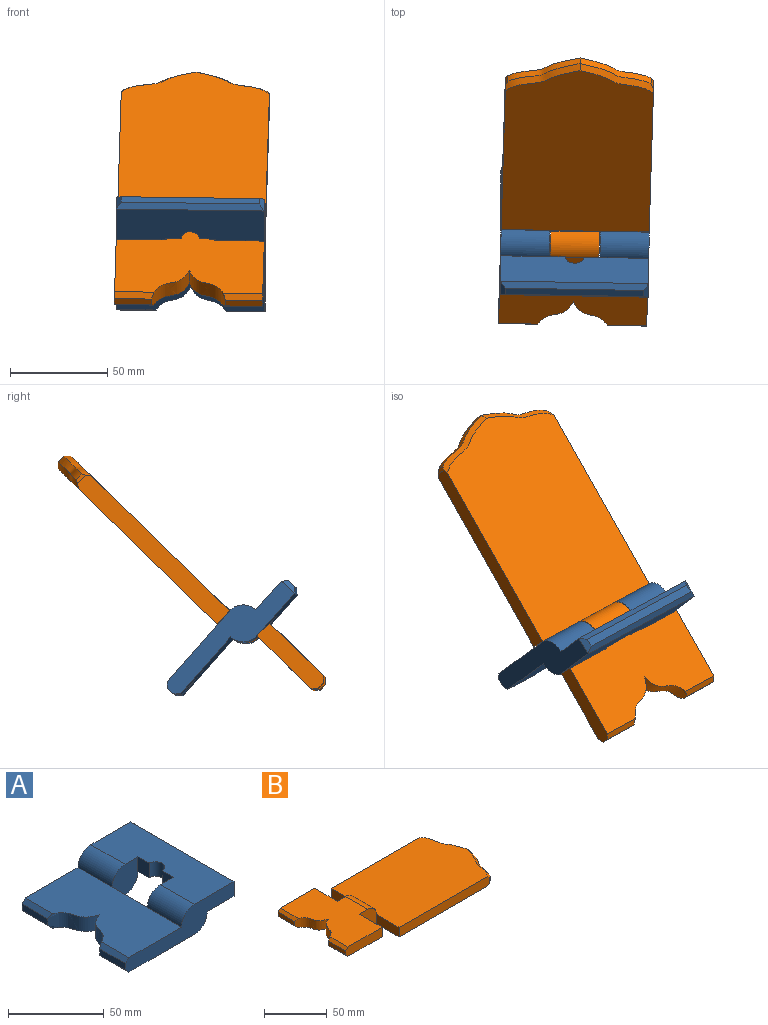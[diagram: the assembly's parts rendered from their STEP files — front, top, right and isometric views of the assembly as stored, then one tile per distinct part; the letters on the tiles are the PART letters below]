
ASSEMBLY  parts=2 mates=1
PART A: 29 faces, bbox 82.6x76.2x19.1 mm
  f0: plane 9.27x8.19mm, normal (-1,0,0), area 75.9mm2, adj f1,f2,f14,f20
  f1: plane 76.2x29.21mm, normal (0,0,1), area 1943.4mm2, adj f0,f7,f10,f12,f13,f14,f16,f17
  f2: plane 76.2x19.69mm, normal (0,0,-1), area 1464.5mm2, adj f0,f6,f8,f12,f13,f14,f16,f17
  f3: plane 76.2x48.97mm, normal (0,0,-1), area 3164.8mm2, adj f6,f8,f12,f13,f14,f15,f17,f18
  f4: plane 76.2x39.45mm, normal (0,0,1), area 2686mm2, adj f7,f10,f12,f13,f14,f15,f17,f18
  f5: plane 19.05x4.19mm, normal (-1,0,0), area 79.8mm2, adj f13,f18,f25,f26
  f6: cylinder r=9.53mm len=25.15mm, axis (0,1,0), area 382.6mm2, adj f2,f3,f12,f17
  f7: cylinder r=9.53mm len=25.15mm, axis (0,1,0), area 382.6mm2, adj f1,f4,f12,f17
  f8: cylinder r=9.53mm len=25.15mm, axis (0,1,0), area 382.6mm2, adj f2,f3,f13,f14
  f9: plane 71.12x4.19mm, normal (1,0,0), area 298.1mm2, adj f21,f22,f23,f24
  f10: cylinder r=9.53mm len=25.15mm, axis (0,1,0), area 382.6mm2, adj f1,f4,f13,f14
  f11: plane 19.05x4.19mm, normal (-1,0,0), area 79.8mm2, adj f12,f19,f27,f28
  f12: plane 80.01x19.05mm, normal (0,-1,0), area 882.7mm2, adj f1,f2,f3,f4,f6,f7,f11,f21
  f13: plane 80.01x19.05mm, normal (0,1,0), area 882.7mm2, adj f1,f2,f3,f4,f5,f8,f10,f24
  f14: plane 19.05x19.05mm, normal (0,-1,0), area 324mm2, adj f0,f1,f2,f3,f4,f8,f10,f15
  f15: plane 25.91x9.27mm, normal (1,0,0), area 240.2mm2, adj f3,f4,f14,f17
  f16: plane 9.27x8.19mm, normal (-1,0,0), area 75.9mm2, adj f1,f2,f17,f20
  f17: plane 19.05x19.05mm, normal (0,1,0), area 324mm2, adj f1,f2,f3,f4,f6,f7,f15,f16
  f18: extruded ~19.05x19.05mm, area 256mm2, adj f3,f4,f5,f19,f25,f26
  f19: extruded ~19.05x19.05mm, area 256mm2, adj f3,f4,f11,f18,f27,f28
  f20: cylinder r=4.76mm len=9.53mm, axis (0,0,1), area 138.7mm2, adj f0,f1,f2,f16
  f21: plane 9.27x2.54mm, normal (0.71,-0.71,0), area 24.2mm2, adj f9,f12,f22,f23
  f22: plane 76.2x2.54mm, normal (0.71,0,0.71), area 264.6mm2, adj f1,f9,f21,f24
  f23: plane 76.2x2.54mm, normal (0.71,0,-0.71), area 264.6mm2, adj f2,f9,f21,f24
  f24: plane 9.27x2.54mm, normal (0.71,0.71,0), area 24.2mm2, adj f9,f13,f22,f23
  f25: plane 20.22x2.54mm, normal (-0.71,0,0.71), area 70.5mm2, adj f4,f5,f13,f18
  f26: plane 20.22x2.54mm, normal (-0.71,0,-0.71), area 70.5mm2, adj f3,f5,f13,f18
  f27: plane 20.22x2.54mm, normal (-0.71,0,-0.71), area 70.5mm2, adj f3,f11,f12,f19
  f28: plane 20.22x2.54mm, normal (-0.71,0,0.71), area 70.5mm2, adj f4,f11,f12,f19
PART B: 37 faces, bbox 179.3x82.2x20 mm
  f0: plane 125.33x77.17mm, normal (0,0,-1), area 8439.3mm2, adj f1,f3,f13,f16,f17,f19,f20,f22
  f1: plane 101.61x9.27mm, normal (0,-1,0), area 938.7mm2, adj f0,f2,f20,f27,f28,f29
  f2: plane 115.81x77.17mm, normal (0,0,1), area 8202mm2, adj f1,f3,f8,f17,f20,f22,f29,f31
  f3: plane 101.61x9.27mm, normal (0,1,0), area 938.7mm2, adj f0,f2,f22,f30,f31,f32
  f4: plane 76.2x48.97mm, normal (0,0,1), area 2922.9mm2, adj f7,f11,f15,f16,f18,f19,f21,f23
  f5: plane 19.05x4.19mm, normal (-1,0,0), area 79.8mm2, adj f15,f23,f33,f34
  f6: plane 76.2x39.45mm, normal (0,0,-1), area 2685.8mm2, adj f7,f9,f15,f18,f21,f23,f24,f34
  f7: plane 41.28x9.27mm, normal (0,-1,0), area 376.2mm2, adj f4,f6,f14,f21,f35,f36
  f8: plane 24.89x0.51mm, normal (1,0,0), area 12.6mm2, adj f2,f10,f16,f19
  f9: plane 24.89x0.51mm, normal (-1,0,0), area 12.6mm2, adj f6,f12,f16,f19
  f10: plane 24.89x0mm, normal (0,0,1), area 0.1mm2, adj f8,f11,f16,f19
  f11: cylinder r=9.53mm len=24.89mm, axis (0,1,0), area 366.1mm2, adj f4,f10,f16,f19
  f12: plane 24.89x0mm, normal (0,0,-1), area 0.1mm2, adj f9,f13,f16,f19
  f13: cylinder r=9.53mm len=24.89mm, axis (0,1,0), area 366.1mm2, adj f0,f12,f16,f19
  f14: plane 19.05x4.19mm, normal (-1,0,0), area 79.8mm2, adj f7,f24,f35,f36
  f15: plane 41.28x9.27mm, normal (0,1,0), area 376.2mm2, adj f4,f5,f6,f18,f33,f34
  f16: plane 19.05x19.05mm, normal (0,1,0), area 324mm2, adj f0,f4,f8,f9,f10,f11,f12,f13
  f17: plane 9.28x0.51mm, normal (-1,0,0), area 4.7mm2, adj f0,f2,f16,f22
  f18: plane 25.65x9.27mm, normal (1,0,0), area 237.8mm2, adj f4,f6,f15,f16
  f19: plane 19.05x19.05mm, normal (0,-1,0), area 324mm2, adj f0,f4,f8,f9,f10,f11,f12,f13
  f20: plane 25.65x9.27mm, normal (-1,0,0), area 237.8mm2, adj f0,f1,f2,f19
  f21: plane 25.65x9.27mm, normal (1,0,0), area 237.8mm2, adj f4,f6,f7,f19
  f22: plane 25.15x9.28mm, normal (-1,0,0), area 233.1mm2, adj f0,f2,f3,f17
  f23: extruded ~19.05x19.05mm, area 255.7mm2, adj f4,f5,f6,f24,f33,f34
  f24: extruded ~19.05x19.05mm, area 255.7mm2, adj f4,f6,f14,f23,f35,f36
  f25: extruded ~37.02x13.79mm, area 167mm2, adj f26,f30,f31,f32
  f26: extruded ~37.02x13.79mm, area 167mm2, adj f25,f27,f28,f29
  f27: plane 6.68x2.66mm, normal (0.46,-0.89,0), area 12.2mm2, adj f1,f26,f28,f29
  f28: bspline ~43.28x19.21mm, area 147.9mm2, adj f0,f1,f26,f27,f30
  f29: bspline ~43.28x19.21mm, area 147.8mm2, adj f1,f2,f26,f27,f31
  f30: bspline ~43.28x19.21mm, area 147.8mm2, adj f0,f3,f25,f28,f32
  f31: bspline ~43.28x19.21mm, area 147.9mm2, adj f2,f3,f25,f29,f32
  f32: plane 6.68x2.66mm, normal (0.46,0.89,0), area 12.2mm2, adj f3,f25,f30,f31
  f33: plane 20.36x2.68mm, normal (-0.71,0,0.71), area 70.5mm2, adj f4,f5,f15,f23
  f34: plane 20.36x2.68mm, normal (-0.71,0,-0.71), area 70.5mm2, adj f5,f6,f15,f23
  f35: plane 20.36x2.68mm, normal (-0.71,0,-0.71), area 70.5mm2, adj f6,f7,f14,f24
  f36: plane 20.36x2.68mm, normal (-0.71,0,0.71), area 70.5mm2, adj f4,f7,f14,f24
PLACE A rot(axis=(0.67,-0.68,0.3),145.3deg) t=(-28.38,-129.87,78.75)mm
PLACE B rot(axis=(0.36,-0.35,0.86),97deg) t=(-28.38,-129.87,78.75)mm
MATE revolute A.f7 <-> B.f13  axis (1,-0.02,-0.01) through (9.72,-130.53,78.24)mm
